# Revit family: Навес с качелями «Орион» Арт 14392
name_source: partatom
category: Антураж
revit_build: Autodesk Revit 2018 (Build: 20180423_1000(x64)
units: mm (PartAtom-declared; Revit-internal decimal feet)

## family parameters
Всегда вертикально = Да
Источник визуального образа = Геометрия семейства
На основе рабочей плоскости = Нет
Общий = Нет
При загрузке вырезать с полостями = Нет
Точка расчета площади = Нет

## types (2) — shared parameters
URL = https://hobbyka.ru
Артикул товара = Арт. 14392
Высота = 2700 мм
Группа модели = Парковые качели
Изготовитель = ООО «Хоббика»
Изображение типоразмера = Навес с качелями «Орион» Арт 14392.jpg
Материал изделия = Сталь, дерево
Цвет каркаса = Сталь
Цвет отделки = Дерево
Ширина = 3000 мм
Ширина подимуа = 3990 мм

## per-type parameters (varying)
| type | Версия 6,0 м | Версия 9,0 м | Длина | Длина подиума | Описание |
| Версия 6,0 м | Да | Нет | 6000 мм | 6920 мм | Навес с качелями «Орион». Модель 6,0 м с двумя качелями |
| Версия 9,0 м | Нет | Да | 9000 мм | 9990 мм | Навес с качелями «Орион». Модель 9,0 м с тремя качелями |
